# Revit family: HL_Корпус плоского душевого лотка InFloor_HL541
name_source: partatom
category: Plumbing Fixtures
revit_build: Autodesk Revit 2016 (Build: 20161004_0715(x64)
units: mm (PartAtom-declared; Revit-internal decimal feet)

## family parameters
Always vertical = Yes
Cut with Voids When Loaded = No
OmniClass Number = 23.70.50.21.24.14
OmniClass Title = Deck Waste Water Drains
Part Type = Normal
Room Calculation Point = Yes
Round Connector Dimension = Use Diameter
Shared = No
Work Plane-Based = No

## types (1)
- HL_Корпус плоского душевого лотка InFloor_HL541
    CW Connection = No
    Description = Душевой трап
    EAN = 9003076048205
    HW Connection = No
    Keynote = HL541
    Manufacturer = HL Hutterer & Lechner GmbH
    Model = HL541
    Type Comments = Душевой трап "PRIMUS-BLUE", в комплект входит "СУХОЙ" сифон, гидроизоляционный комплект для жидкой гидроизоляции, монтажные уголки для регулировки по высоте, монтажная заглушка и надставной элемент с подрамником.
    URL = http://www.hutterer-lechner.com
    Vent Connection = No
    Waste Connection = Yes
    ВЕС = 1,12 kg
    ВЫСОТА МОНТАЖА = 62-200mm (Estrichoberkante)
    МАКСИМАЛЬНАЯ НАГРУЗКА КЛАССА = K3 - 300kg
    МАТЕРИАЛ = PP/Edelstahl
    НАСАДКА = Edelstahl V4A 10-30mm/121x121
    ПРОИЗВОДИТЕЛЬНОСТЬ = 0,47l/s
    РАЗМЕР = DN40/50
    РЕШЁТКА = Edelstahl V2A 115x115mm
    решётка_тип = HL_Pешётка_HL037Pr.1E

## geometry (parser evidence)
native form markers: Sweep x23
no freeform markers — native parametric forms only
